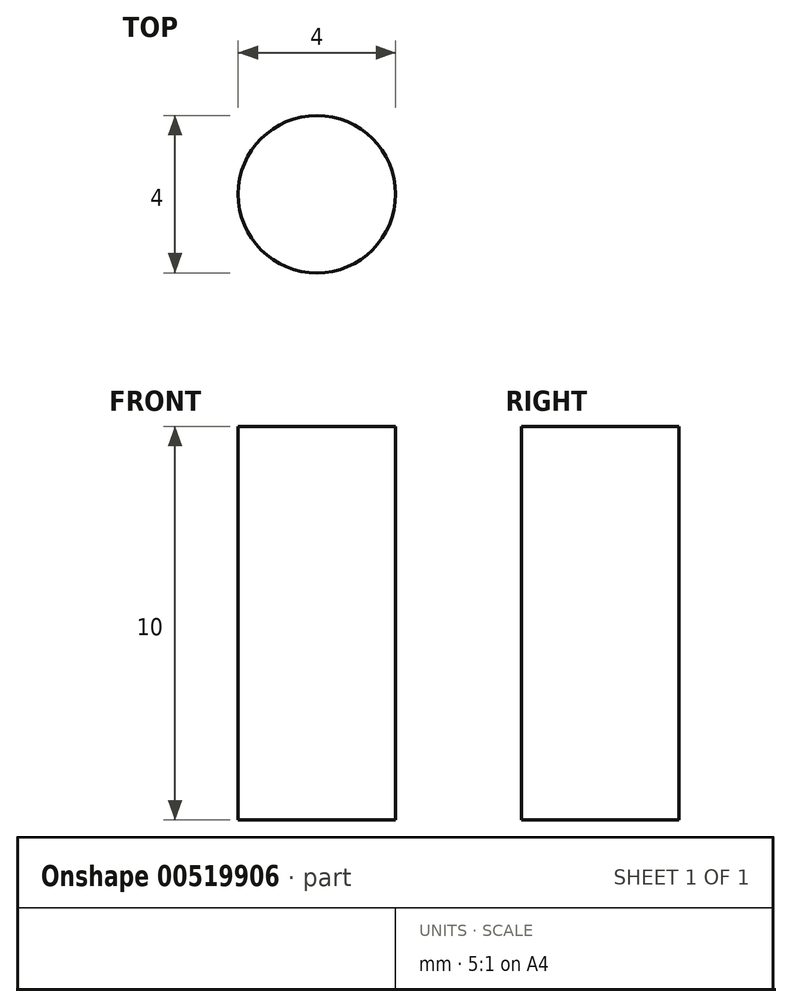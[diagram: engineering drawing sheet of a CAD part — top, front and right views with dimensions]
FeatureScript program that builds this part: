
annotation { "Feature Type Name" : "Feature", "Feature Type Description" : "" }
export const myFeature = defineFeature(function(context is Context, id is Id, definition is map)
    precondition{}
    {
        {
            var Q0;
            Q0=qCreatedBy(makeId("Top.planeOp"),FACE);
            var sketch = newSketch(context, id + "F0", { "sketchPlane" : qUnion([Q0])});
            skCircle(sketch, "E0", {"center": v(0, 0) * mm, "radius": 2 * mm});
            skSolve(sketch);
        }
        {
            var Q0;
            Q0 = qSketchRegion(id + "F0", true);
            extrude(context, id + "F1", {"entities" : qUnion([Q0]), "depth" : 10 * mm, "offsetDistance" : 25 * mm});
        }
    });
